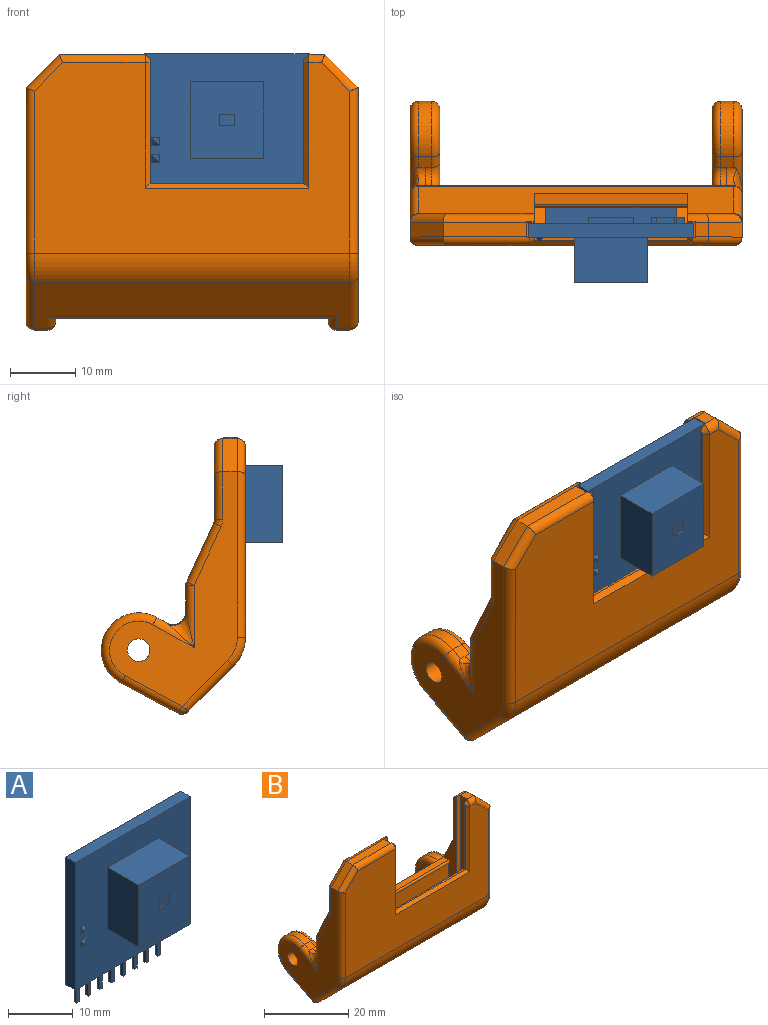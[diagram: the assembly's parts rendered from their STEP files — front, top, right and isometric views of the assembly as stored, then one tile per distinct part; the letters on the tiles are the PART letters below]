
ASSEMBLY  parts=2 mates=1
PART A: 91 faces, bbox 25.1x11.6x29.8 mm
  f0: plane 11.68x11.18mm, normal (0,-1,0), area 126.5mm2, adj f7,f8,f9,f10,f11,f12,f13,f14
  f1: plane 25.15x24.13mm, normal (0,-1,0), area 473mm2, adj f2,f3,f4,f5,f7,f8,f9,f10
  f2: plane 24.13x2.16mm, normal (1,0,0), area 52.1mm2, adj f1,f3,f5,f6
  f3: plane 25.15x2.16mm, normal (0,0,1), area 54.3mm2, adj f1,f2,f4,f6
  f4: plane 24.13x2.16mm, normal (-1,0,0), area 52.1mm2, adj f1,f3,f5,f6
  f5: plane 25.15x2.16mm, normal (0,0,-1), area 54.3mm2, adj f1,f2,f4,f6
  f6: plane 25.15x24.13mm, normal (0,1,0), area 476.1mm2, adj f2,f3,f4,f5,f16,f17,f18,f19
  f7: plane 11.18x6.86mm, normal (0,0,-1), area 76.6mm2, adj f0,f1,f8,f10
  f8: plane 11.68x6.86mm, normal (1,0,0), area 80.1mm2, adj f0,f1,f7,f9
  f9: plane 11.18x6.86mm, normal (0,0,1), area 76.6mm2, adj f0,f1,f8,f10
  f10: plane 11.68x6.86mm, normal (-1,0,0), area 80.1mm2, adj f0,f1,f7,f9
  f11: plane 2.29x0.25mm, normal (0,0,1), area 0.6mm2, adj f0,f12,f14,f15
  f12: plane 1.78x0.25mm, normal (-1,0,0), area 0.5mm2, adj f0,f11,f13,f15
  f13: plane 2.29x0.25mm, normal (0,0,-1), area 0.6mm2, adj f0,f12,f14,f15
  f14: plane 1.78x0.25mm, normal (1,0,0), area 0.5mm2, adj f0,f11,f13,f15
  f15: plane 2.29x1.78mm, normal (0,-1,0), area 4.1mm2, adj f11,f12,f13,f14
  f16: plane 6.86x0.94mm, normal (0,0,-1), area 6.4mm2, adj f6,f17,f19,f20
  f17: plane 4.06x0.94mm, normal (-1,0,0), area 3.8mm2, adj f6,f16,f18,f20
  f18: plane 6.86x0.94mm, normal (0,0,1), area 6.4mm2, adj f6,f17,f19,f20
  f19: plane 4.06x0.94mm, normal (1,0,0), area 3.8mm2, adj f6,f16,f18,f20
  f20: plane 6.86x4.06mm, normal (0,1,0), area 27.9mm2, adj f16,f17,f18,f19
  f21: plane 2.79x0.94mm, normal (0,0,-1), area 2.6mm2, adj f6,f22,f24,f25
  f22: plane 3.81x0.94mm, normal (-1,0,0), area 3.6mm2, adj f6,f21,f23,f25
  f23: plane 2.79x0.94mm, normal (0,0,1), area 2.6mm2, adj f6,f22,f24,f25
  f24: plane 3.81x0.94mm, normal (1,0,0), area 3.6mm2, adj f6,f21,f23,f25
  f25: plane 3.81x2.79mm, normal (0,1,0), area 10.6mm2, adj f21,f22,f23,f24
  f26: plane 3.43x0.94mm, normal (0,0,-1), area 3.2mm2, adj f6,f27,f29,f30
  f27: plane 2.54x0.94mm, normal (-1,0,0), area 2.4mm2, adj f6,f26,f28,f30
  f28: plane 3.43x0.94mm, normal (0,0,1), area 3.2mm2, adj f6,f27,f29,f30
  f29: plane 2.54x0.94mm, normal (1,0,0), area 2.4mm2, adj f6,f26,f28,f30
  f30: plane 3.43x2.54mm, normal (0,1,0), area 8.7mm2, adj f26,f27,f28,f29
  f31: plane 1.7x0.94mm, normal (1,0,0), area 1.6mm2, adj f6,f32,f34,f35
  f32: plane 1.27x0.94mm, normal (0,0,-1), area 1.2mm2, adj f6,f31,f33,f35
  f33: plane 1.7x0.94mm, normal (-1,0,0), area 1.6mm2, adj f6,f32,f34,f35
  f34: plane 1.27x0.94mm, normal (0,0,1), area 1.2mm2, adj f6,f31,f33,f35
  f35: plane 1.7x1.27mm, normal (0,1,0), area 2.2mm2, adj f31,f32,f33,f34
  f36: plane 20x2.54mm, normal (0,0,-1), area 48.3mm2, adj f6,f37,f39,f40,f41,f42,f43,f44
  f37: plane 4.06x2.54mm, normal (-1,0,0), area 10.3mm2, adj f6,f36,f38,f40
  f38: plane 20x2.54mm, normal (0,0,1), area 50.8mm2, adj f6,f37,f39,f40
  f39: plane 4.06x2.54mm, normal (1,0,0), area 10.3mm2, adj f6,f36,f38,f40
  f40: plane 20x4.06mm, normal (0,1,0), area 81.3mm2, adj f36,f37,f38,f39
  f41: plane 6.99x0.56mm, normal (0,1,0), area 3.9mm2, adj f36,f42,f44,f45
  f42: plane 6.99x0.56mm, normal (1,0,0), area 3.9mm2, adj f36,f41,f43,f45
  f43: plane 6.99x0.56mm, normal (0,-1,0), area 3.9mm2, adj f36,f42,f44,f45
  f44: plane 6.99x0.56mm, normal (-1,0,0), area 3.9mm2, adj f36,f41,f43,f45
  f45: plane 0.56x0.56mm, normal (0,0,-1), area 0.3mm2, adj f41,f42,f43,f44
  f46: plane 6.99x0.56mm, normal (0,-1,0), area 3.9mm2, adj f36,f47,f49,f50
  f47: plane 6.99x0.56mm, normal (-1,0,0), area 3.9mm2, adj f36,f46,f48,f50
  f48: plane 6.99x0.56mm, normal (0,1,0), area 3.9mm2, adj f36,f47,f49,f50
  f49: plane 6.99x0.56mm, normal (1,0,0), area 3.9mm2, adj f36,f46,f48,f50
  f50: plane 0.56x0.56mm, normal (0,0,-1), area 0.3mm2, adj f46,f47,f48,f49
  f51: plane 6.99x0.56mm, normal (0,1,0), area 3.9mm2, adj f36,f52,f54,f55
  f52: plane 6.99x0.56mm, normal (1,0,0), area 3.9mm2, adj f36,f51,f53,f55
  f53: plane 6.99x0.56mm, normal (0,-1,0), area 3.9mm2, adj f36,f52,f54,f55
  f54: plane 6.99x0.56mm, normal (-1,0,0), area 3.9mm2, adj f36,f51,f53,f55
  f55: plane 0.56x0.56mm, normal (0,0,-1), area 0.3mm2, adj f51,f52,f53,f54
  f56: plane 6.99x0.56mm, normal (0,1,0), area 3.9mm2, adj f36,f57,f59,f60
  f57: plane 6.99x0.56mm, normal (1,0,0), area 3.9mm2, adj f36,f56,f58,f60
  f58: plane 6.99x0.56mm, normal (0,-1,0), area 3.9mm2, adj f36,f57,f59,f60
  f59: plane 6.99x0.56mm, normal (-1,0,0), area 3.9mm2, adj f36,f56,f58,f60
  f60: plane 0.56x0.56mm, normal (0,0,-1), area 0.3mm2, adj f56,f57,f58,f59
  f61: plane 6.99x0.56mm, normal (0,1,0), area 3.9mm2, adj f36,f62,f64,f65
  f62: plane 6.99x0.56mm, normal (1,0,0), area 3.9mm2, adj f36,f61,f63,f65
  f63: plane 6.99x0.56mm, normal (0,-1,0), area 3.9mm2, adj f36,f62,f64,f65
  f64: plane 6.99x0.56mm, normal (-1,0,0), area 3.9mm2, adj f36,f61,f63,f65
  f65: plane 0.56x0.56mm, normal (0,0,-1), area 0.3mm2, adj f61,f62,f63,f64
  f66: plane 6.99x0.56mm, normal (1,0,0), area 3.9mm2, adj f36,f67,f69,f70
  f67: plane 6.99x0.56mm, normal (0,-1,0), area 3.9mm2, adj f36,f66,f68,f70
  f68: plane 6.99x0.56mm, normal (-1,0,0), area 3.9mm2, adj f36,f67,f69,f70
  f69: plane 6.99x0.56mm, normal (0,1,0), area 3.9mm2, adj f36,f66,f68,f70
  f70: plane 0.56x0.56mm, normal (0,0,-1), area 0.3mm2, adj f66,f67,f68,f69
  f71: plane 6.99x0.56mm, normal (1,0,0), area 3.9mm2, adj f36,f72,f74,f75
  f72: plane 6.99x0.56mm, normal (0,-1,0), area 3.9mm2, adj f36,f71,f73,f75
  f73: plane 6.99x0.56mm, normal (-1,0,0), area 3.9mm2, adj f36,f72,f74,f75
  f74: plane 6.99x0.56mm, normal (0,1,0), area 3.9mm2, adj f36,f71,f73,f75
  f75: plane 0.56x0.56mm, normal (0,0,-1), area 0.3mm2, adj f71,f72,f73,f74
  f76: plane 6.99x0.56mm, normal (1,0,0), area 3.9mm2, adj f36,f77,f79,f80
  f77: plane 6.99x0.56mm, normal (0,-1,0), area 3.9mm2, adj f36,f76,f78,f80
  f78: plane 6.99x0.56mm, normal (-1,0,0), area 3.9mm2, adj f36,f77,f79,f80
  f79: plane 6.99x0.56mm, normal (0,1,0), area 3.9mm2, adj f36,f76,f78,f80
  f80: plane 0.56x0.56mm, normal (0,0,-1), area 0.3mm2, adj f76,f77,f78,f79
  f81: plane 1.27x0.51mm, normal (0,-0.71,-0.71), area 0.5mm2, adj f1,f82,f84,f85
  f82: plane 1.27x0.51mm, normal (0.71,-0.71,0), area 0.5mm2, adj f1,f81,f83,f85
  f83: plane 1.27x0.51mm, normal (0,-0.71,0.71), area 0.5mm2, adj f1,f82,f84,f85
  f84: plane 1.27x0.51mm, normal (-0.71,-0.71,0), area 0.5mm2, adj f1,f81,f83,f85
  f85: plane 0.25x0.25mm, normal (0,-1,0), area 0.1mm2, adj f81,f82,f83,f84
  f86: plane 1.27x0.51mm, normal (0,-0.71,-0.71), area 0.5mm2, adj f1,f87,f89,f90
  f87: plane 1.27x0.51mm, normal (0.71,-0.71,0), area 0.5mm2, adj f1,f86,f88,f90
  f88: plane 1.27x0.51mm, normal (0,-0.71,0.71), area 0.5mm2, adj f1,f87,f89,f90
  f89: plane 1.27x0.51mm, normal (-0.71,-0.71,0), area 0.5mm2, adj f1,f86,f88,f90
  f90: plane 0.25x0.25mm, normal (0,-1,0), area 0.1mm2, adj f86,f87,f88,f89
PART B: 105 faces, bbox 51.2x23.5x42.6 mm
  f0: plane 38.89x7.96mm, normal (1,0,0), area 128.6mm2, adj f11,f12,f13,f15,f16,f20,f30,f36
  f1: cylinder r=1.27mm len=2.03mm, axis (-1,0,0), area 3.3mm2, adj f5,f24,f68,f97
  f2: cylinder r=1.91mm len=2.83mm, axis (-1,0,0), area 3.8mm2, adj f4,f20,f82,f90
  f3: cylinder r=5.71mm len=10.76mm, axis (-1,0,0), area 36.7mm2, adj f4,f5,f61,f94
  f4: plane 2.07x1.66mm, normal (0,-0.48,0.87), area 3.8mm2, adj f2,f3,f58,f82,f92
  f5: plane 8.72x4.64mm, normal (0,0.47,-0.88), area 20.1mm2, adj f1,f3,f65,f96
  f6: cylinder r=1.73mm len=4.57mm, axis (1,0,0), area 49.6mm2, adj f26,f84
  f7: cylinder r=1.91mm len=2.83mm, axis (-1,0,0), area 3.8mm2, adj f8,f19,f20,f85
  f8: bspline ~2.91x1.99mm, area 4.9mm2, adj f7,f9,f19,f20,f62,f66
  f9: bspline ~5.08x3.87mm, area 4.4mm2, adj f8,f62,f66
  f10: bspline ~5.08x3.87mm, area 4.4mm2, adj f54,f58,f82
  f11: plane 23.5x1.72mm, normal (0,0,1), area 40.3mm2, adj f0,f15,f34,f98
  f12: plane 24.38x1.14mm, normal (0,-1,0), area 27.9mm2, adj f0,f13,f29,f44
  f13: plane 2.41x1.14mm, normal (0,0,1), area 2.8mm2, adj f0,f12,f29,f30
  f14: plane 23.5x0.41mm, normal (0,0,1), area 9.7mm2, adj f30,f31,f32,f78
  f15: plane 48.26x9.02mm, normal (0,0.91,0.42), area 305mm2, adj f0,f11,f34,f43,f47,f48,f55,f56
  f16: plane 17.72x11.15mm, normal (0,1,0), area 188.2mm2, adj f0,f44,f46,f48,f49
  f17: plane 2.22x2.1mm, normal (0,0,1), area 4.7mm2, adj f33,f37,f40,f50
  f18: cylinder r=5.71mm len=10.76mm, axis (-1,0,0), area 36.7mm2, adj f19,f25,f69,f87
  f19: plane 2.07x1.66mm, normal (0,-0.48,0.87), area 3.8mm2, adj f7,f8,f18,f66,f86
  f20: plane 48.69x17.02mm, normal (0,1,0), area 448.2mm2, adj f0,f2,f7,f8,f34,f54,f55,f62
  f21: plane 11.15x7.05mm, normal (0,1,0), area 69.2mm2, adj f34,f40,f41,f42,f43
  f22: plane 12.76x2.22mm, normal (0,0,1), area 28.4mm2, adj f29,f38,f44,f63
  f23: plane 48.26x29.12mm, normal (0,-1,0), area 906.7mm2, adj f39,f50,f53,f57,f63,f67,f70,f77
  f24: plane 48.26x6.96mm, normal (0,-0.71,-0.71), area 359.5mm2, adj f1,f39,f64,f71,f75,f91,f93,f95
  f25: plane 8.72x4.64mm, normal (0,0.47,-0.88), area 20.1mm2, adj f18,f71,f72,f88
  f26: plane 35.86x19.53mm, normal (1,0,0), area 250.7mm2, adj f6,f37,f42,f45,f47,f54,f57,f58
  f27: plane 35.86x19.53mm, normal (-1,0,0), area 250.7mm2, adj f38,f49,f52,f56,f62,f66,f69,f70
  f28: plane 24.38x1.14mm, normal (0,-1,0), area 27.9mm2, adj f33,f34,f35,f40
  f29: plane 24.38x2.41mm, normal (1,0,0), area 58.8mm2, adj f12,f13,f22,f30,f44,f63
  f30: plane 32.42x25.82mm, normal (0,1,0), area 353.4mm2, adj f0,f13,f14,f29,f31,f32,f33,f34
  f31: plane 18.91x0.41mm, normal (1,0,0), area 7.8mm2, adj f14,f30,f76,f77
  f32: plane 18.91x0.41mm, normal (-1,0,0), area 7.8mm2, adj f14,f30,f79,f80
  f33: plane 24.38x2.41mm, normal (-1,0,0), area 58.8mm2, adj f17,f28,f30,f35,f40,f50
  f34: plane 38.89x7.96mm, normal (-1,0,0), area 128.6mm2, adj f11,f15,f20,f21,f28,f30,f35,f36
  f35: plane 2.41x1.14mm, normal (0,0,1), area 2.8mm2, adj f28,f30,f33,f34
  f36: plane 23.5x6.38mm, normal (0,-1,0), area 149.9mm2, adj f0,f34,f98,f102
  f37: plane 5.08x5.08mm, normal (0.71,0,0.71), area 16mm2, adj f17,f26,f41,f53
  f38: plane 5.08x5.08mm, normal (-0.71,0,0.71), area 16mm2, adj f22,f27,f46,f67
  f39: cylinder r=6.35mm len=48.26mm, axis (-1,0,0), area 240.7mm2, adj f23,f24,f60,f73
  f40: cylinder r=1.27mm len=3.24mm, axis (1,0,0), area 6mm2, adj f17,f21,f28,f33,f34,f41
  f41: cylinder r=1.27mm len=5.98mm, axis (0.71,0,-0.71), area 13.3mm2, adj f21,f37,f40,f42
  f42: cylinder r=1.27mm len=7.34mm, axis (0,0,-1), area 14.1mm2, adj f21,f26,f41,f45
  f43: cylinder r=1.27mm len=7.05mm, axis (1,0,0), area 3.9mm2, adj f15,f21,f34,f45
  f44: cylinder r=1.27mm len=13.91mm, axis (1,0,0), area 27.3mm2, adj f0,f12,f16,f22,f29,f46
  f45: torus R=2.54mm, axis (1,0,0), area 1.5mm2, adj f26,f42,f43,f47
  f46: cylinder r=1.27mm len=5.98mm, axis (-0.71,0,-0.71), area 13.3mm2, adj f16,f38,f44,f49
  f47: cylinder r=1.27mm len=9.55mm, axis (0,0.42,-0.91), area 19.8mm2, adj f15,f26,f45,f51
  f48: cylinder r=1.27mm len=17.72mm, axis (1,0,0), area 9.7mm2, adj f0,f15,f16,f52
  f49: cylinder r=1.27mm len=7.34mm, axis (0,0,1), area 14.1mm2, adj f16,f27,f46,f52
  f50: cylinder r=1.27mm len=2.48mm, axis (-1,0,0), area 4.5mm2, adj f17,f23,f30,f33,f53,f80
  f51: sphere r=1.27mm, area 0.7mm2, adj f47,f54,f55
  f52: torus R=2.54mm, axis (1,0,0), area 1.5mm2, adj f27,f48,f49,f56
  f53: cylinder r=1.27mm len=5.98mm, axis (0.71,0,-0.71), area 13.3mm2, adj f23,f37,f50,f57
  f54: cylinder r=1.27mm len=9.5mm, axis (0,0,-1), area 12.1mm2, adj f10,f20,f26,f51,f82
  f55: cylinder r=1.27mm len=48.26mm, axis (-1,0,0), area 26.4mm2, adj f15,f20,f51,f59
  f56: cylinder r=1.27mm len=9.55mm, axis (0,-0.42,0.91), area 19.8mm2, adj f15,f27,f52,f59
  f57: cylinder r=1.27mm len=25.31mm, axis (0,0,1), area 50mm2, adj f23,f26,f53,f60
  f58: cylinder r=1.27mm len=6.94mm, axis (0,0.87,0.48), area 7.6mm2, adj f4,f10,f26,f61,f82
  f59: sphere r=1.27mm, area 0.5mm2, adj f55,f56,f62
  f60: torus R=5.08mm, axis (1,0,0), area 9.2mm2, adj f26,f39,f57,f64
  f61: torus R=4.45mm, axis (1,0,0), area 33.1mm2, adj f3,f26,f58,f65
  f62: cylinder r=1.27mm len=9.5mm, axis (0,0,1), area 12.1mm2, adj f8,f9,f20,f27,f59
  f63: cylinder r=1.27mm len=13.14mm, axis (-1,0,0), area 25.8mm2, adj f22,f23,f29,f30,f67,f76
  f64: cylinder r=1.27mm len=7.86mm, axis (0,-0.71,0.71), area 19.6mm2, adj f24,f26,f60,f68
  f65: cylinder r=1.27mm len=9.31mm, axis (0,-0.88,-0.47), area 19.7mm2, adj f5,f26,f61,f68
  f66: cylinder r=1.27mm len=6.94mm, axis (0,-0.87,-0.48), area 7.6mm2, adj f8,f9,f19,f27,f69
  f67: cylinder r=1.27mm len=5.98mm, axis (-0.71,0,-0.71), area 13.3mm2, adj f23,f38,f63,f70
  f68: sphere r=1.27mm, area 2mm2, adj f1,f64,f65
  f69: torus R=4.45mm, axis (1,0,0), area 33.1mm2, adj f18,f27,f66,f72
  f70: cylinder r=1.27mm len=25.31mm, axis (0,0,-1), area 50mm2, adj f23,f27,f67,f73
  f71: cylinder r=1.27mm len=2.03mm, axis (-1,0,0), area 3.3mm2, adj f24,f25,f74,f89
  f72: cylinder r=1.27mm len=9.31mm, axis (0,0.88,0.47), area 19.7mm2, adj f25,f27,f69,f74
  f73: torus R=5.08mm, axis (1,0,0), area 9.2mm2, adj f27,f39,f70,f75
  f74: sphere r=1.27mm, area 2.5mm2, adj f71,f72,f75
  f75: cylinder r=1.27mm len=7.86mm, axis (0,0.71,-0.71), area 19.6mm2, adj f24,f27,f73,f74
  f76: cone r=0.51mm half-angle=45deg, axis (-1,0,0), area 1.4mm2, adj f30,f31,f63,f77
  f77: plane 19.18x0.76mm, normal (0.71,-0.71,0), area 20.3mm2, adj f23,f31,f76,f78
  f78: plane 25.02x0.76mm, normal (0,-0.71,0.71), area 26.1mm2, adj f14,f23,f77,f79
  f79: plane 19.18x0.76mm, normal (-0.71,-0.71,0), area 20.3mm2, adj f23,f32,f78,f80
  f80: cone r=0.51mm half-angle=45deg, axis (1,0,0), area 1.4mm2, adj f30,f32,f50,f79
  f81: cylinder r=1.73mm len=4.57mm, axis (1,0,0), area 49.6mm2, adj f27,f83
  f82: bspline ~2.91x1.99mm, area 4.9mm2, adj f2,f4,f10,f20,f54,f58
  f83: plane 13x12.03mm, normal (1,0,0), area 96.4mm2, adj f20,f81,f85,f86,f87,f88,f91,f93
  f84: plane 13x12.03mm, normal (-1,0,0), area 96.4mm2, adj f6,f20,f90,f92,f93,f94,f95,f96
  f85: torus R=3.17mm, axis (-1,0,0), area 7.4mm2, adj f7,f20,f83,f86
  f86: cylinder r=1.27mm len=2.23mm, axis (0,0.87,0.48), area 3.7mm2, adj f19,f83,f85,f87
  f87: torus R=4.45mm, axis (-1,0,0), area 33.1mm2, adj f18,f83,f86,f88
  f88: cylinder r=1.27mm len=9.31mm, axis (0,-0.88,-0.47), area 19.7mm2, adj f25,f83,f87,f89
  f89: sphere r=1.27mm, area 2.1mm2, adj f71,f88,f91
  f90: torus R=3.17mm, axis (-1,0,0), area 7.4mm2, adj f2,f20,f84,f92
  f91: cylinder r=1.27mm len=2.75mm, axis (0,0.71,-0.71), area 4mm2, adj f24,f83,f89,f93
  f92: cylinder r=1.27mm len=2.23mm, axis (0,-0.87,-0.48), area 3.7mm2, adj f4,f84,f90,f94
  f93: cylinder r=1.27mm len=44.2mm, axis (1,0,0), area 127.2mm2, adj f20,f24,f83,f84,f91,f95
  f94: torus R=4.45mm, axis (-1,0,0), area 33.1mm2, adj f3,f84,f92,f96
  f95: cylinder r=1.27mm len=2.75mm, axis (0,-0.71,0.71), area 4mm2, adj f24,f84,f93,f97
  f96: cylinder r=1.27mm len=9.31mm, axis (0,0.88,0.47), area 19.7mm2, adj f5,f84,f94,f97
  f97: sphere r=1.27mm, area 2.1mm2, adj f1,f95,f96
  f98: cylinder r=0.38mm len=23.5mm, axis (1,0,0), area 28.1mm2, adj f0,f11,f34,f36
  f99: plane 23.5x5.33mm, normal (0,0.71,0.71), area 177mm2, adj f0,f34,f100,f104
  f100: plane 23.5x1.16mm, normal (0,-0.12,0.99), area 27.4mm2, adj f0,f34,f99,f103
  f101: plane 23.5x0.93mm, normal (0,0.54,-0.84), area 26mm2, adj f0,f20,f34,f102
  f102: cylinder r=1.27mm len=23.5mm, axis (-1,0,0), area 63.8mm2, adj f0,f34,f36,f101
  f103: cylinder r=1.27mm len=23.5mm, axis (-1,0,0), area 50.4mm2, adj f0,f20,f34,f100
  f104: cylinder r=1.27mm len=23.5mm, axis (1,0,0), area 2mm2, adj f0,f30,f34,f99
PLACE A t=(5.33,0.95,10.29)mm
PLACE B at identity fixed
MATE planar A.f1 <-> B.f30  axis (0,-1,0) through (5.33,-1.21,-1.78)mm
